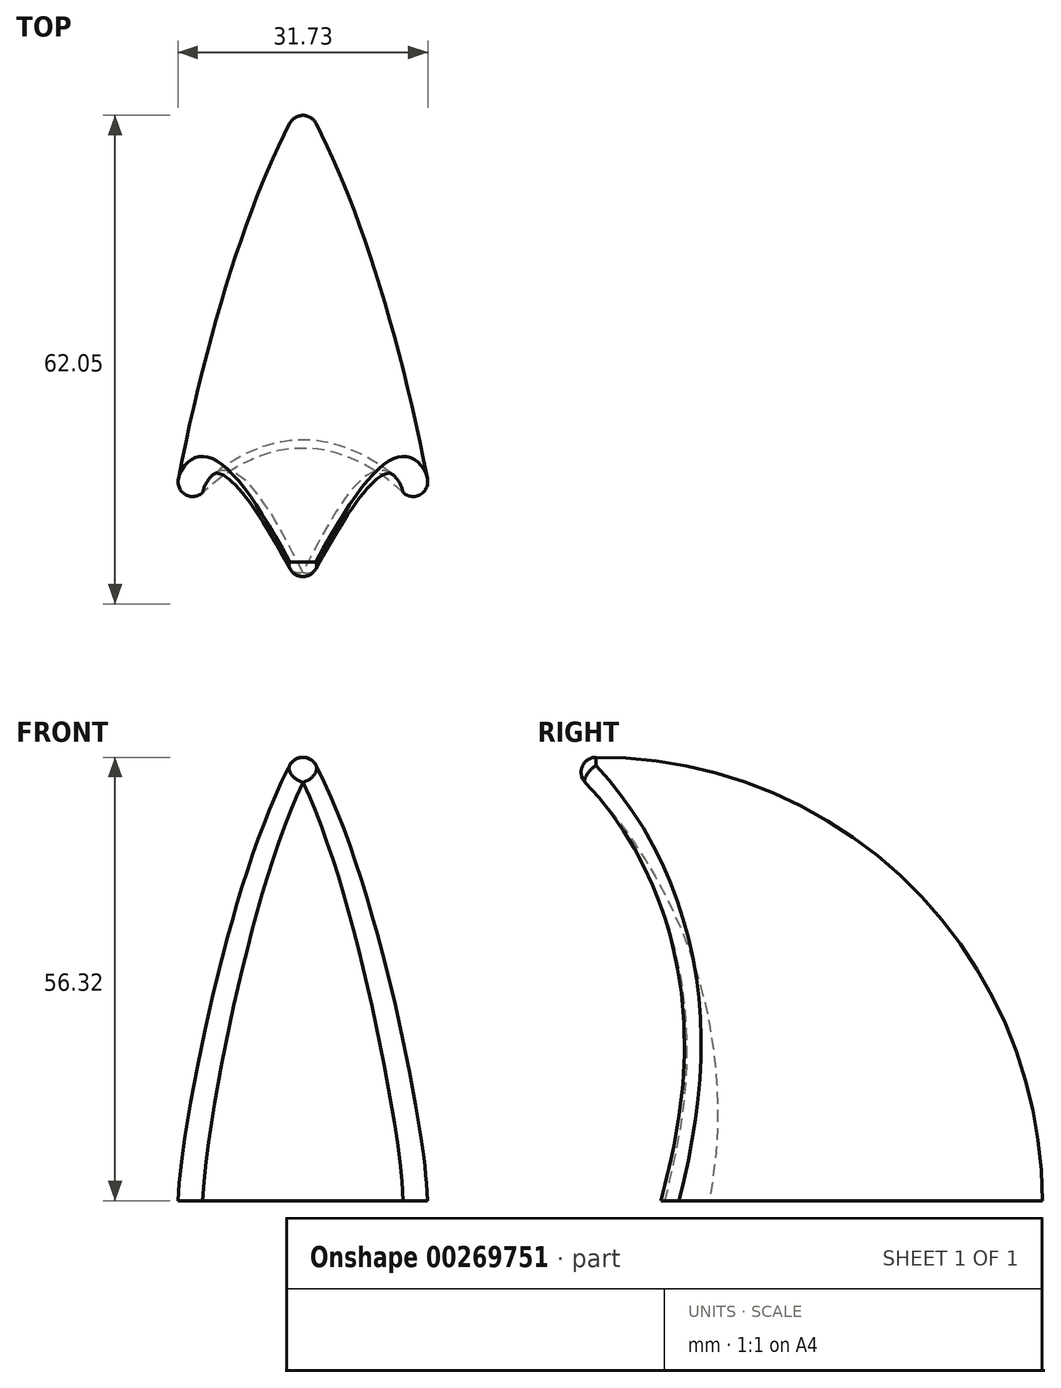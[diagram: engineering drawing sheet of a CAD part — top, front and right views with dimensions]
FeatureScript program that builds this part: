
annotation { "Feature Type Name" : "Feature", "Feature Type Description" : "" }
export const myFeature = defineFeature(function(context is Context, id is Id, definition is map)
    precondition{}
    {
        {
            var Q0;
            Q0=qCreatedBy(makeId("Top.planeOp"),FACE);
            var sketch = newSketch(context, id + "F0", { "sketchPlane" : qUnion([Q0])});
            skEllipticalArc(sketch, "E0", {});
            skLineSegment(sketch, "E1", {"start": v(-23.46, 0) * mm, "end": v(23.46, 0) * mm});
            skEllipticalArc(sketch, "E2.MirrorCS", {});
            skPoint(sketch, "E3.orphan", {"position": v(23.46, 0) * mm});
            skPoint(sketch, "E4.visualSharp", {"position": v(0, 77.8) * mm});
            skArc(sketch, "E4.filletArc", {"start": v(2.22, 73.74) * mm, "mid": v(0, 75.1) * mm, "end": v(-2.22, 73.74) * mm});
            const initialGuessF0  = {"E0": [0, 0, -0.16370247110655353, 0.9865097571507381, 0.09187502934078014, 0.023161781502507094, 4.6705794622368275, 5.619741885800852], "E2.MirrorCS": [0, 0, 0.16370247110655353, 0.9865097571507381, 0.09187502934078014, 0.023161781502507094, 0.6634434213787351, 1.6126058449427587]};
            skSetInitialGuess(sketch, initialGuessF0);
            skSolve(sketch);
        }
        {
            var Q0;
            Q0=qCreatedBy(makeId("Top.planeOp"),FACE);
            var sketch = newSketch(context, id + "F1", { "sketchPlane" : qUnion([Q0])});
            skEllipticalArc(sketch, "E5", {});
            skLineSegment(sketch, "E6", {"start": v(-40.68, -140.7) * mm, "end": v(40.68, -140.7) * mm});
            const initialGuessF1  = {"E5": [0, -0.14069192111492157, 0, 1, 0.08080634676819629, 0.04068115038200901, 4.71238898038469, 1.5707963267948966]};
            skSetInitialGuess(sketch, initialGuessF1);
            skSolve(sketch);
        }
        {
            var Q0;
            Q0=makeQuery(id+"F0.imprint","IMPRINT",FACE,{"disambiguationData":[TD([[makeQuery(id+"F0.imprint","IMPRINT",EDGE,{"derivedFrom":sQuery(id+"F0.wireOp",EDGE,"E0")}),1.0]])]});
            var Q1;
            Q1=sQuery(id+"F0.wireOp",EDGE,"E1");
            revolve(context, id + "F2", {"entities" : qUnion([Q0]), "axis" : qUnion([Q1]), "revolveType" : RevolveType.ONE_DIRECTION, "angle" : 180 * degree});
        }
        {
            var Q0;
            Q0=makeQuery(id+"F1.imprint","IMPRINT",FACE,{"disambiguationData":[TD([[makeQuery(id+"F1.imprint","IMPRINT",EDGE,{"derivedFrom":sQuery(id+"F1.wireOp",EDGE,"E5")}),1.0]])]});
            var Q1;
            Q1=sQuery(id+"F1.wireOp",EDGE,"E6");
            revolve(context, id + "F3", {"entities" : qUnion([Q0]), "axis" : qUnion([Q1]), "revolveType" : RevolveType.FULL});
        }
        {
            var Q0;
            Q0=makeQuery(id+"F3.opRevolve","SWEPT_BODY",BODY,{"disambiguationData":[OSD([sQuery(id+"F1.wireOp",EDGE,"E5"),sQuery(id+"F1.wireOp",EDGE,"E6")])]});
            transform(context, id + "F4", {"entities" : qUnion([Q0]), "transformType" : TransformType.TRANSLATION_3D, "dx" : 0 * mm, "dy" : 80 * mm, "dz" : 15 * mm, "makeCopy" : false});
        }
        {
            var Q0;
            Q0=makeQuery(id+"F3.opRevolve","SWEPT_BODY",BODY,{"disambiguationData":[OSD([sQuery(id+"F1.wireOp",EDGE,"E5"),sQuery(id+"F1.wireOp",EDGE,"E6")])]});
            var Q1;
            Q1=makeQuery(id+"F2.opRevolve","SWEPT_BODY",BODY,{"disambiguationData":[OSD([sQuery(id+"F0.wireOp",EDGE,"E0"),sQuery(id+"F0.wireOp",EDGE,"E1")])]});
            booleanBodies(context, id + "F5", {"operationType" : BooleanOperationType.SUBTRACTION, "tools" : qUnion([Q0]), "targets" : qUnion([Q1])});
        }
        {
            var Q0;
            Q0=makeQuery(id+"F5.opBoolean","INTERSECT",EDGE,{"derivedFrom":[makeQuery(id+"F2.opRevolve","SWEPT_FACE",FACE,{"disambiguationData":[OSD([sQuery(id+"F0.wireOp",EDGE,"E0")])]}),makeQuery(id+"F3.opRevolve","SWEPT_FACE",FACE,{"disambiguationData":[OSD([sQuery(id+"F1.wireOp",EDGE,"E5")])]})]});
            fillet(context, id + "F6", {"entities" : qUnion([Q0]), "radius" : 2.5 * mm, "tangentPropagation" : true, "allowEdgeOverflow" : false});
        }
        {
            var Q0;
            Q0=makeQuery(id+"F2.opRevolve","SWEPT_BODY",BODY,{"disambiguationData":[OSD([sQuery(id+"F0.wireOp",EDGE,"E0"),sQuery(id+"F0.wireOp",EDGE,"E1"),sQuery(id+"F0.wireOp",EDGE,"E2.MirrorCS"),sQuery(id+"F0.wireOp",EDGE,"E4.filletArc")])]});
            var Q1;
            Q1=makeQuery(id+"F2.opRevolve","CAP_VERTEX",VERTEX,{"disambiguationData":[OSD([sQuery(id+"F0.wireOp",EDGE,"E0"),sQuery(id+"F0.wireOp",EDGE,"E4.filletArc")])],"isStart":true});
            transform(context, id + "F7", {"entities" : qUnion([Q0]), "transformType" : TransformType.SCALE_UNIFORMLY, "scale" : 0.75, "scalePoint" : qUnion([Q1]), "makeCopy" : false});
        }
    });
